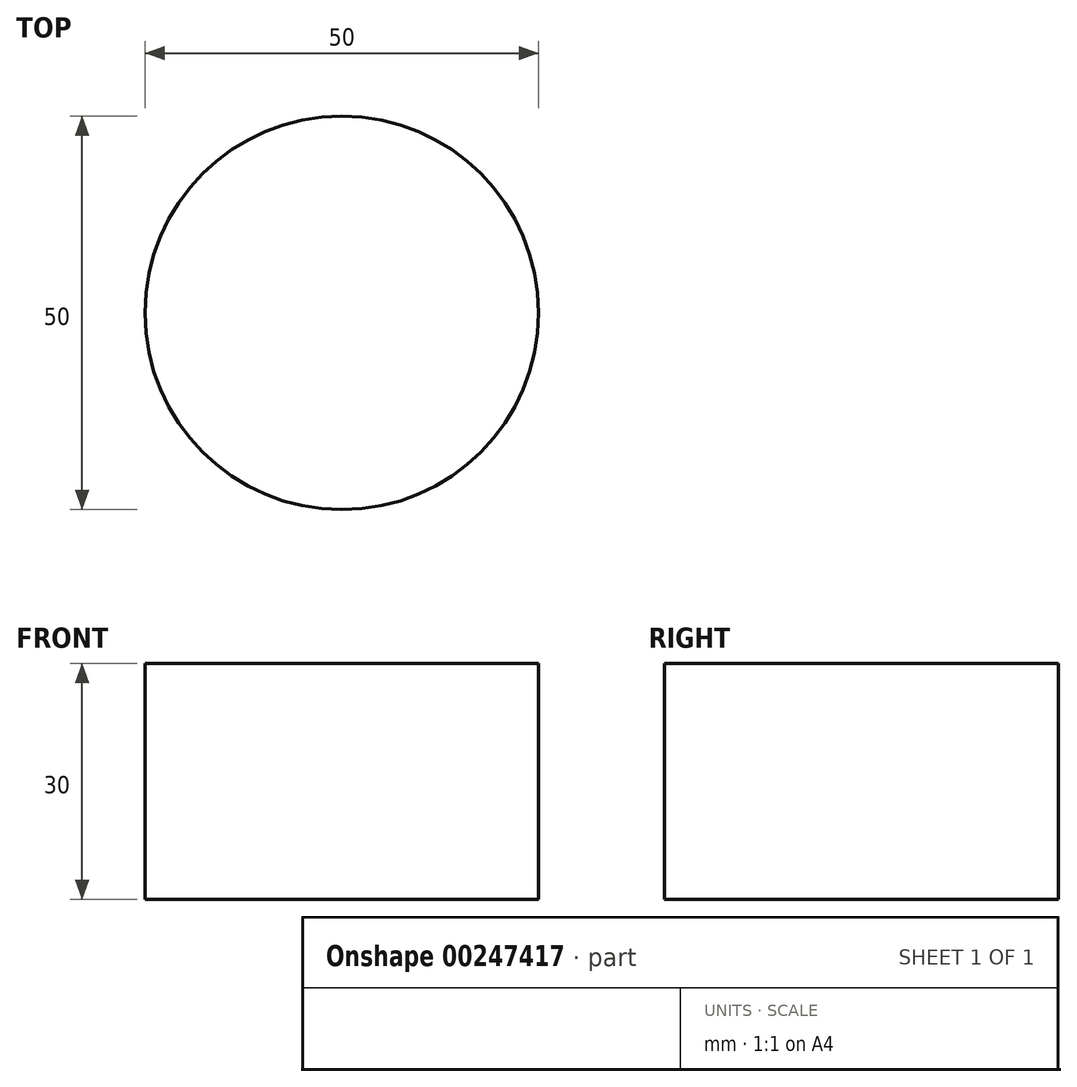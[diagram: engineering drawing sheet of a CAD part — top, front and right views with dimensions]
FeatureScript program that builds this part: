
annotation { "Feature Type Name" : "Feature", "Feature Type Description" : "" }
export const myFeature = defineFeature(function(context is Context, id is Id, definition is map)
    precondition{}
    {
        {
            var Q0;
            Q0=qCreatedBy(makeId("Top.planeOp"),FACE);
            var sketch = newSketch(context, id + "F0", { "sketchPlane" : qUnion([Q0])});
            skCircle(sketch, "E0", {"center": v(0, 2.01) * mm, "radius": 25 * mm});
            skSolve(sketch);
        }
        {
            var Q0;
            Q0 = qSketchRegion(id + "F0", true);
            extrude(context, id + "F1", {"entities" : qUnion([Q0]), "depth" : 30 * mm, "offsetDistance" : 25 * mm});
        }
    });
